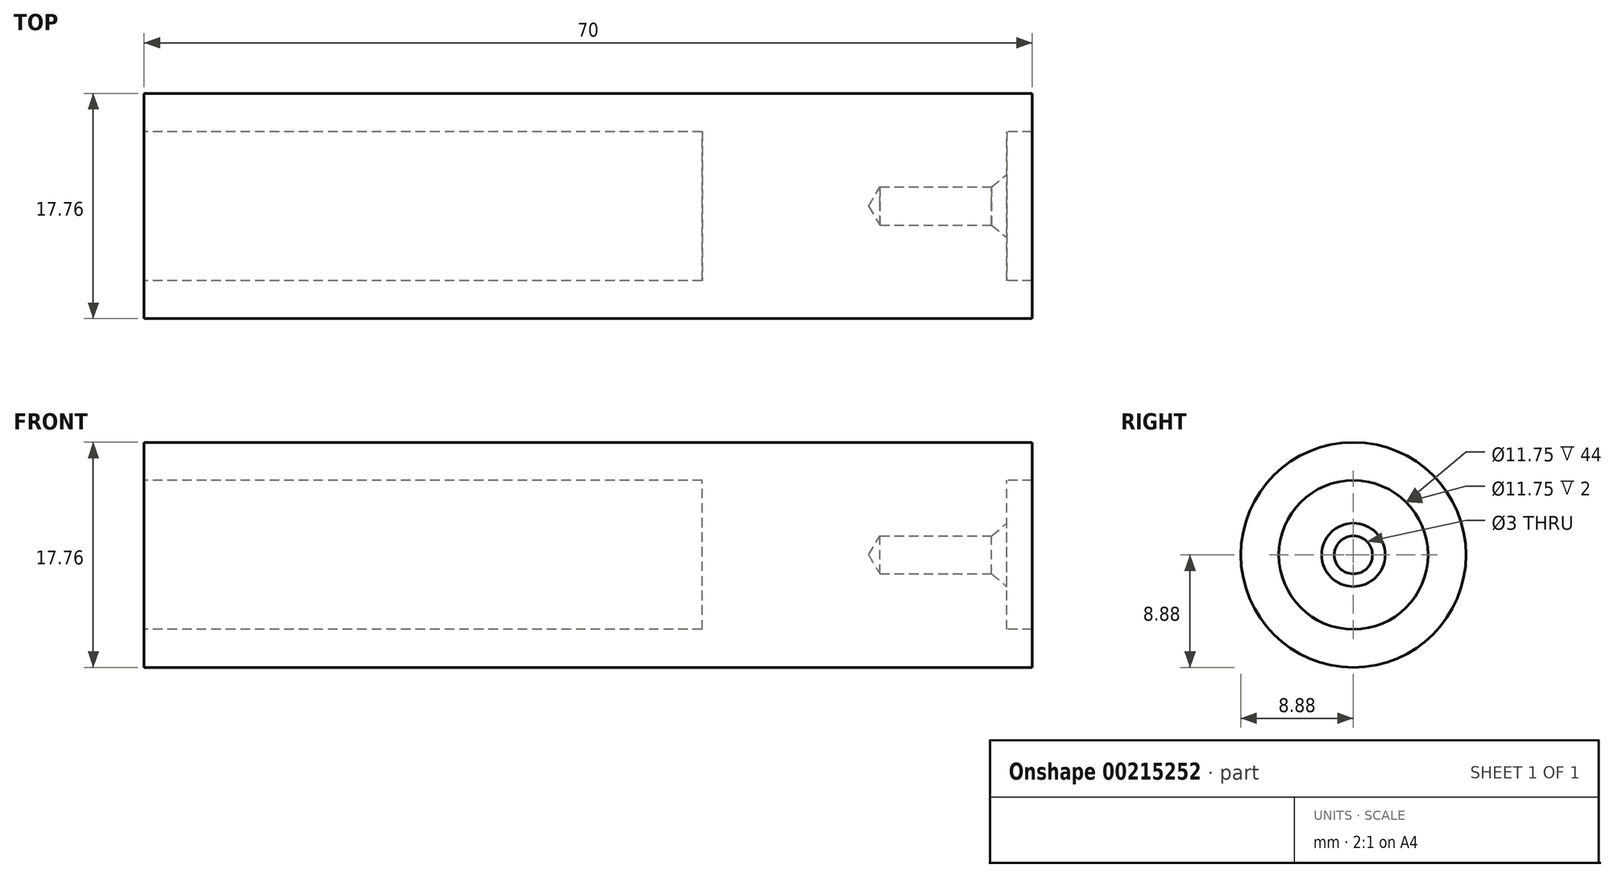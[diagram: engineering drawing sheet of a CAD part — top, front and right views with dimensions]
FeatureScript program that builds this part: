
annotation { "Feature Type Name" : "Feature", "Feature Type Description" : "" }
export const myFeature = defineFeature(function(context is Context, id is Id, definition is map)
    precondition{}
    {
        {
            var Q0;
            Q0=qCreatedBy(makeId("Right.planeOp"),FACE);
            var sketch = newSketch(context, id + "F0", { "sketchPlane" : qUnion([Q0])});
            skCircle(sketch, "E0", {"center": v(0, 0) * mm, "radius": 8.88 * mm});
            skCircle(sketch, "E1", {"center": v(0, 0) * mm, "radius": 5.88 * mm});
            skSolve(sketch);
        }
        {
            var Q0;
            Q0 = qSketchRegion(id + "F0", true);
            extrude(context, id + "F1", {"entities" : qUnion([Q0]), "depth" : 70 * mm});
        }
        {
            var Q0;
            Q0=makeQuery(id+"F0.imprint","IMPRINT",FACE,{"disambiguationData":[TD([[makeQuery(id+"F0.imprint","IMPRINT",EDGE,{"derivedFrom":sQuery(id+"F0.wireOp",EDGE,"E1")}),1.0]])]});
            extrude(context, id + "F2", {"entities" : qUnion([Q0]), "operationType" : NewBodyOperationType.ADD, "depth" : 68 * mm, "hasSecondDirection" : true, "secondDirectionOppositeDirection" : false, "secondDirectionDepth" : 44 * mm});
        }
        {
            var Q0;
            Q0=makeQuery(id+"F2.opExtrude","CAP_FACE",FACE,{"disambiguationData":[OSD([sQuery(id+"F0.wireOp",EDGE,"E1")])],"isStart":false});
            var sketch = newSketch(context, id + "F3", { "sketchPlane" : qUnion([Q0])});
            skPoint(sketch, "E2", {"position": v(0, 0) * mm});
            skSolve(sketch);
        }
        {
            var Q0;
            Q0=sQuery(id+"F3.wireOp",VERTEX,"E2");
            var Q1;
            Q1=makeQuery(id+"F1.opExtrude","SWEPT_BODY",BODY,{"disambiguationData":[OSD([sQuery(id+"F0.wireOp",EDGE,"E0"),sQuery(id+"F0.wireOp",EDGE,"E1")])]});
            hole(context, id + "F4", {"style" : HoleStyle.C_SINK, "endStyle" : HoleEndStyle.BLIND, "holeDiameter" : 3 * mm, "cSinkDiameter" : 5 * mm, "cSinkAngle" : 80 * degree, "holeDepth" : 10 * mm, "startFromSketch" : true, "locations" : qUnion([Q0]), "scope" : qUnion([Q1])});
        }
    });
